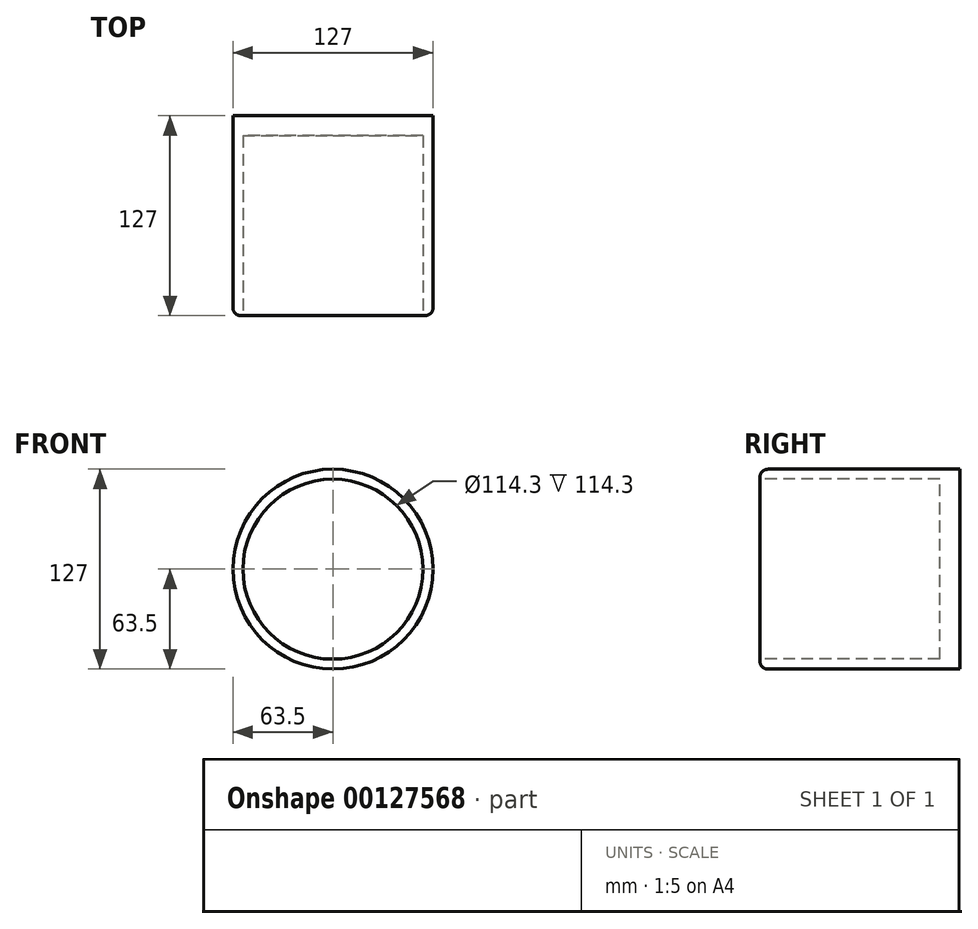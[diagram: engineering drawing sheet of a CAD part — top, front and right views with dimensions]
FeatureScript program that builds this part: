
annotation { "Feature Type Name" : "Feature", "Feature Type Description" : "" }
export const myFeature = defineFeature(function(context is Context, id is Id, definition is map)
    precondition{}
    {
        {
            var Q0;
            Q0=qCreatedBy(makeId("Front.planeOp"),FACE);
            var sketch = newSketch(context, id + "F0", { "sketchPlane" : qUnion([Q0])});
            skCircle(sketch, "E0", {"center": v(0, 0) * mm, "radius": 63.5 * mm});
            skSolve(sketch);
        }
        {
            var Q0;
            Q0=qSketchRegion(id+"F0",true);
            extrude(context, id + "F1", {"entities" : qUnion([Q0]), "depth" : 127 * mm});
        }
        {
            var Q0;
            Q0=makeQuery(id+"F1.opExtrude","CAP_FACE",FACE,{"disambiguationData":[OSD([sQuery(id+"F0.wireOp",EDGE,"E0")])],"isStart":false});
            var sketch = newSketch(context, id + "F2", { "sketchPlane" : qUnion([Q0])});
            skCircle(sketch, "E1.0", {"center": v(0, 0) * mm, "radius": 57.15 * mm});
            skSolve(sketch);
        }
        {
            var Q0;
            Q0=makeQuery(id+"F2.imprint","IMPRINT",FACE,{"disambiguationData":[TD([[makeQuery(id+"F2.imprint","IMPRINT",EDGE,{"derivedFrom":sQuery(id+"F2.wireOp",EDGE,"E1.0")}),1.0]])]});
            extrude(context, id + "F3", {"entities" : qUnion([Q0]), "operationType" : NewBodyOperationType.REMOVE, "oppositeDirection" : true, "depth" : 114.3 * mm});
        }
        {
            var Q0;
            Q0=makeQuery(id+"F1.opExtrude","CAP_EDGE",EDGE,{"disambiguationData":[OSD([sQuery(id+"F0.wireOp",EDGE,"E0")])],"isStart":false});
            fillet(context, id + "F4", {"entities" : qUnion([Q0]), "radius" : 5.08 * mm, "tangentPropagation" : true, "allowEdgeOverflow" : false});
        }
    });
